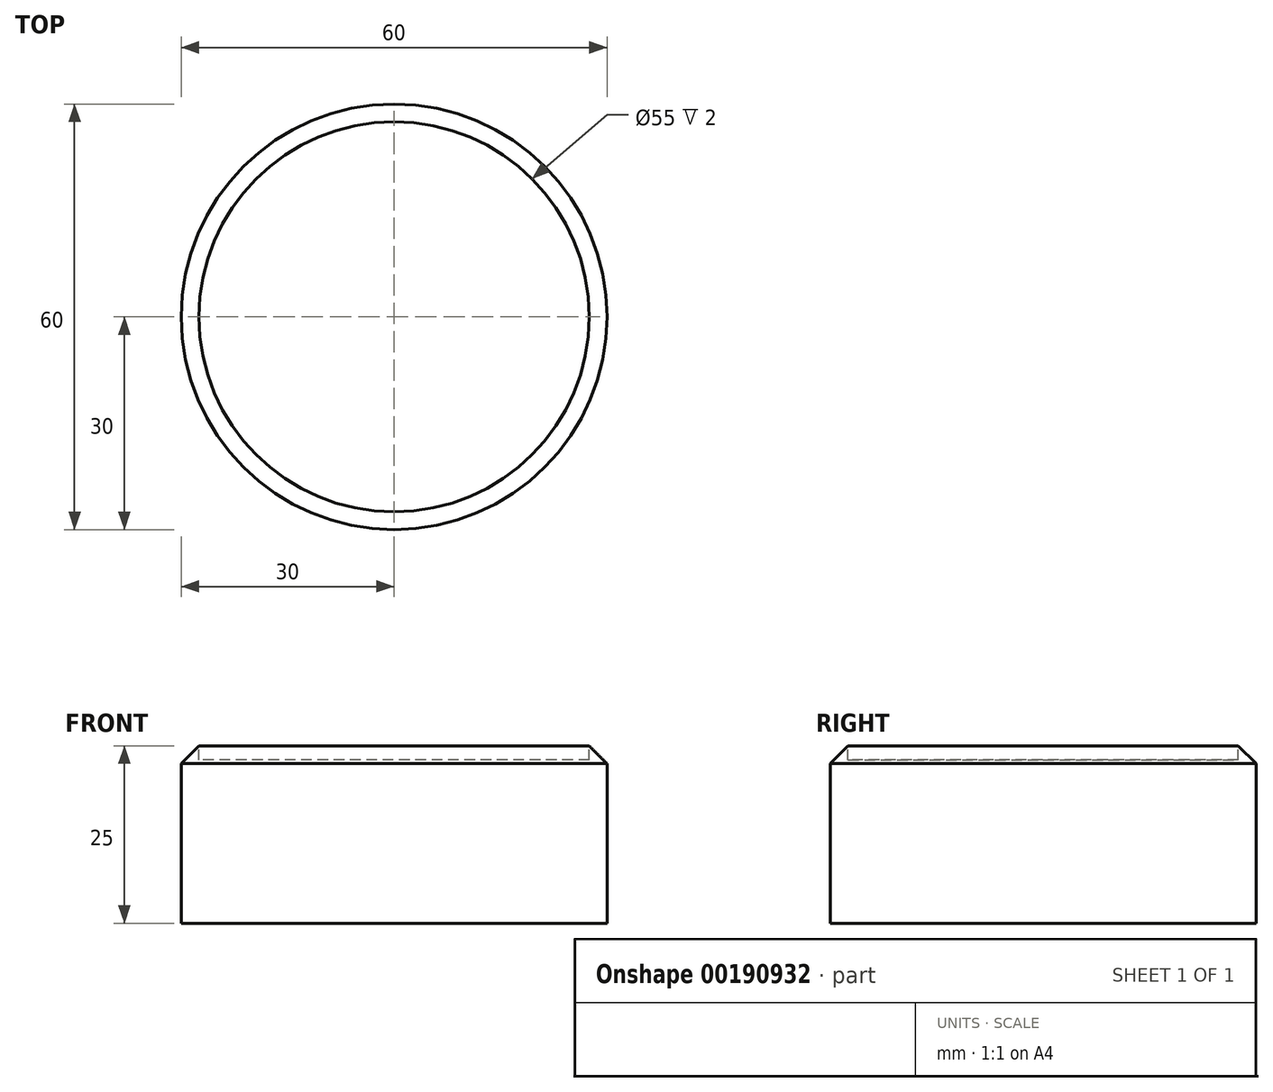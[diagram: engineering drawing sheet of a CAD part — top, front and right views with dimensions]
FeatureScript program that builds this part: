
annotation { "Feature Type Name" : "Feature", "Feature Type Description" : "" }
export const myFeature = defineFeature(function(context is Context, id is Id, definition is map)
    precondition{}
    {
        {
            var Q0;
            Q0=qCreatedBy(makeId("Top.planeOp"),FACE);
            var sketch = newSketch(context, id + "F0", { "sketchPlane" : qUnion([Q0])});
            skCircle(sketch, "E0", {"center": v(0, 0) * mm, "radius": 30 * mm});
            skSolve(sketch);
        }
        {
            var Q0;
            Q0 = qSketchRegion(id + "F0", true);
            extrude(context, id + "F1", {"entities" : qUnion([Q0]), "depth" : 25 * mm});
        }
        {
            var Q0;
            Q0=makeQuery(id+"F1.opExtrude","CAP_EDGE",EDGE,{"disambiguationData":[OSD([sQuery(id+"F0.wireOp",EDGE,"E0")])],"isStart":false});
            chamfer(context, id + "F2", {"entities" : qUnion([Q0]), "width" : 2.5 * mm, "tangentPropagation" : true});
        }
        {
            var Q0;
            Q0=makeQuery(id+"F1.opExtrude","CAP_FACE",FACE,{"disambiguationData":[OSD([sQuery(id+"F0.wireOp",EDGE,"E0")])],"isStart":false});
            extrude(context, id + "F3", {"entities" : qUnion([Q0]), "oppositeDirection" : true, "depth" : 2 * mm});
        }
        {
            var Q0;
            Q0=makeQuery(id+"F3.opExtrude","SWEPT_BODY",BODY,{"disambiguationData":[OSD([sQuery(id+"F0.wireOp",EDGE,"E0")])]});
            var Q1;
            Q1=makeQuery(id+"F1.opExtrude","SWEPT_BODY",BODY,{"disambiguationData":[OSD([sQuery(id+"F0.wireOp",EDGE,"E0")])]});
            booleanBodies(context, id + "F4", {"operationType" : BooleanOperationType.SUBTRACTION, "tools" : qUnion([Q0]), "targets" : qUnion([Q1]), "keepTools" : true});
        }
    });
